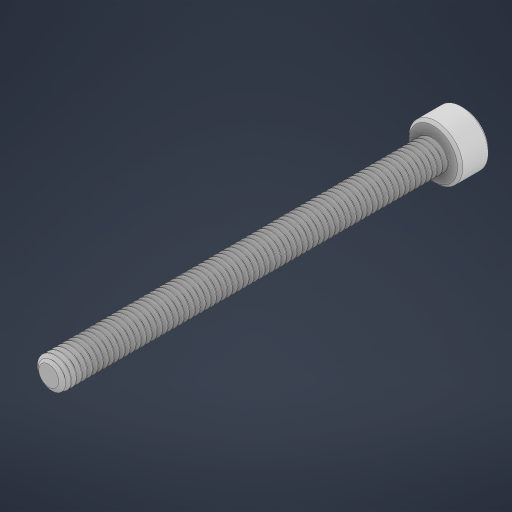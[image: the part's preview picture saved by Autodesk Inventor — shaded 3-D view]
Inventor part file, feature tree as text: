
AUTODESK INVENTOR PART (.ipt)
format: ipt  version: 2023 (Build 270158000, 158)  size: 1,913,344 bytes
history: native  units: in
note: dims shown in document units (in); Inventor stores cm internally (conversion verified against a paired STEP export)
features: chamfer x1
ambient origin geometry x8: Origin, YZ Plane, XZ Plane, XY Plane, X Axis, Y Axis, Z Axis, Center Point
bodies: Solid1 (feature_tree)
feature tree (1):
  chamfer  "Chamfer1"  [1 undecoded]
note: 1 required parameter value undecoded (feature->parameter linkage not recoverable at this tier; creation-order binding heuristic only, values carry confidence <= 0.55)
